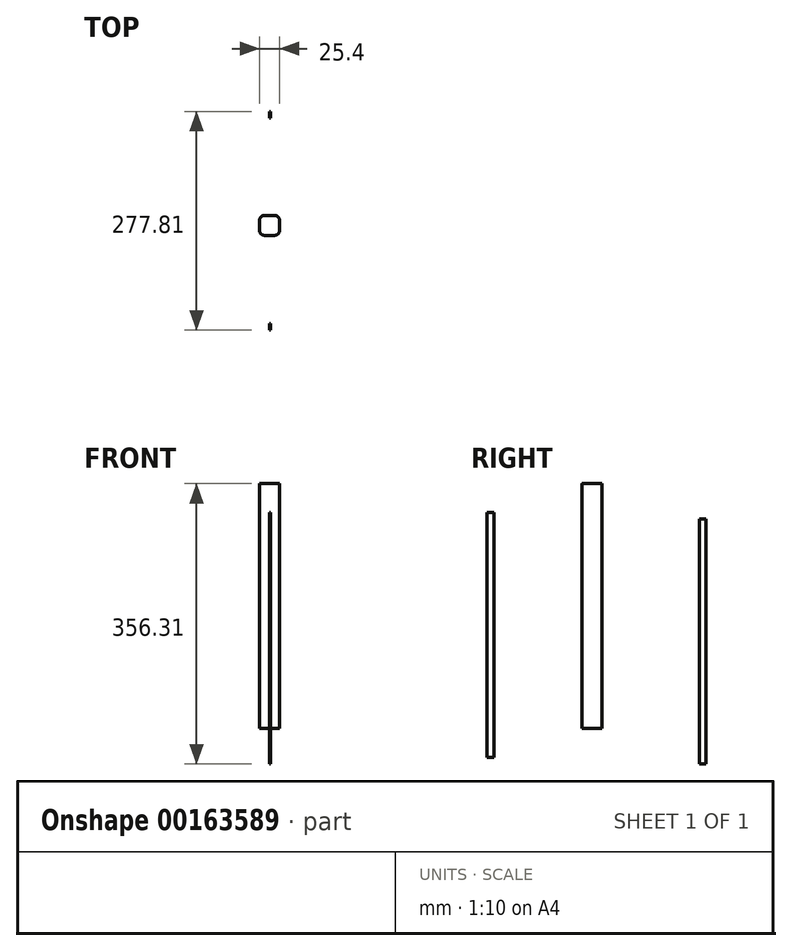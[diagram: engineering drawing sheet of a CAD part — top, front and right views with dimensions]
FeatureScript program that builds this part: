
annotation { "Feature Type Name" : "Feature", "Feature Type Description" : "" }
export const myFeature = defineFeature(function(context is Context, id is Id, definition is map)
    precondition{}
    {
        {
            var Q0;
            Q0=qCreatedBy(makeId("Top.planeOp"),FACE);
            var sketch = newSketch(context, id + "F0", { "sketchPlane" : qUnion([Q0])});
            skLineSegment(sketch, "E0.bottom", {"start": v(6.35, 12.7) * mm, "end": v(-6.35, 12.7) * mm});
            skLineSegment(sketch, "E0.top", {"start": v(6.35, -12.7) * mm, "end": v(-6.35, -12.7) * mm});
            skLineSegment(sketch, "E0.left", {"start": v(12.7, 6.35) * mm, "end": v(12.7, -6.35) * mm});
            skLineSegment(sketch, "E0.right", {"start": v(-12.7, 6.35) * mm, "end": v(-12.7, -6.35) * mm});
            skPoint(sketch, "E0.middle", {"position": v(0, 0) * mm});
            skPoint(sketch, "E1.visualSharp", {"position": v(-12.7, 12.7) * mm});
            skArc(sketch, "E1.filletArc", {"start": v(-6.35, 12.7) * mm, "mid": v(-10.84, 10.84) * mm, "end": v(-12.7, 6.35) * mm});
            skPoint(sketch, "E2.visualSharp", {"position": v(-12.7, -12.7) * mm});
            skArc(sketch, "E2.filletArc", {"start": v(-12.7, -6.35) * mm, "mid": v(-10.84, -10.84) * mm, "end": v(-6.35, -12.7) * mm});
            skPoint(sketch, "E3.visualSharp", {"position": v(12.7, -12.7) * mm});
            skArc(sketch, "E3.filletArc", {"start": v(6.35, -12.7) * mm, "mid": v(10.84, -10.84) * mm, "end": v(12.7, -6.35) * mm});
            skPoint(sketch, "E4.visualSharp", {"position": v(12.7, 12.7) * mm});
            skArc(sketch, "E4.filletArc", {"start": v(12.7, 6.35) * mm, "mid": v(10.84, 10.84) * mm, "end": v(6.35, 12.7) * mm});
            skSolve(sketch);
        }
        {
            var Q0;
            Q0=qSketchRegion(id+"F0",true);
            extrude(context, id + "F1", {"entities" : qUnion([Q0]), "depth" : 311.15 * mm});
        }
        {
            var Q0;
            Q0=qCreatedBy(makeId("Right.planeOp"),FACE);
            var sketch = newSketch(context, id + "F2", { "sketchPlane" : qUnion([Q0])});
            skLineSegment(sketch, "E5.bottom", {"start": v(-133.08, 274.33) * mm, "end": v(-124.62, 274.33) * mm});
            skLineSegment(sketch, "E5.top", {"start": v(-133.08, -36.82) * mm, "end": v(-124.62, -36.82) * mm});
            skLineSegment(sketch, "E5.left", {"start": v(-133.08, 274.33) * mm, "end": v(-133.08, -36.82) * mm});
            skLineSegment(sketch, "E5.right", {"start": v(-124.62, 274.33) * mm, "end": v(-124.62, -36.82) * mm});
            skSolve(sketch);
        }
        {
            var Q0;
            Q0=makeQuery(id+"F2.imprint","IMPRINT",FACE,{"disambiguationData":[TD([[makeQuery(id+"F2.imprint","IMPRINT",EDGE,{"derivedFrom":sQuery(id+"F2.wireOp",EDGE,"E5.bottom")}),-1.0]])]});
            extrude(context, id + "F3", {"entities" : qUnion([Q0]), "depth" : 1.27 * mm});
        }
        {
            var Q0;
            Q0=qCreatedBy(makeId("Right.planeOp"),FACE);
            var sketch = newSketch(context, id + "F4", { "sketchPlane" : qUnion([Q0])});
            skLineSegment(sketch, "E6.bottom", {"start": v(136.27, 265.99) * mm, "end": v(144.73, 265.99) * mm});
            skLineSegment(sketch, "E6.top", {"start": v(136.27, -45.16) * mm, "end": v(144.73, -45.16) * mm});
            skLineSegment(sketch, "E6.left", {"start": v(136.27, 265.99) * mm, "end": v(136.27, -45.16) * mm});
            skLineSegment(sketch, "E6.right", {"start": v(144.73, 265.99) * mm, "end": v(144.73, -45.16) * mm});
            skSolve(sketch);
        }
        {
            var Q0;
            Q0 = qSketchRegion(id + "F4", true);
            extrude(context, id + "F5", {"entities" : qUnion([Q0]), "depth" : 1.27 * mm});
        }
    });
